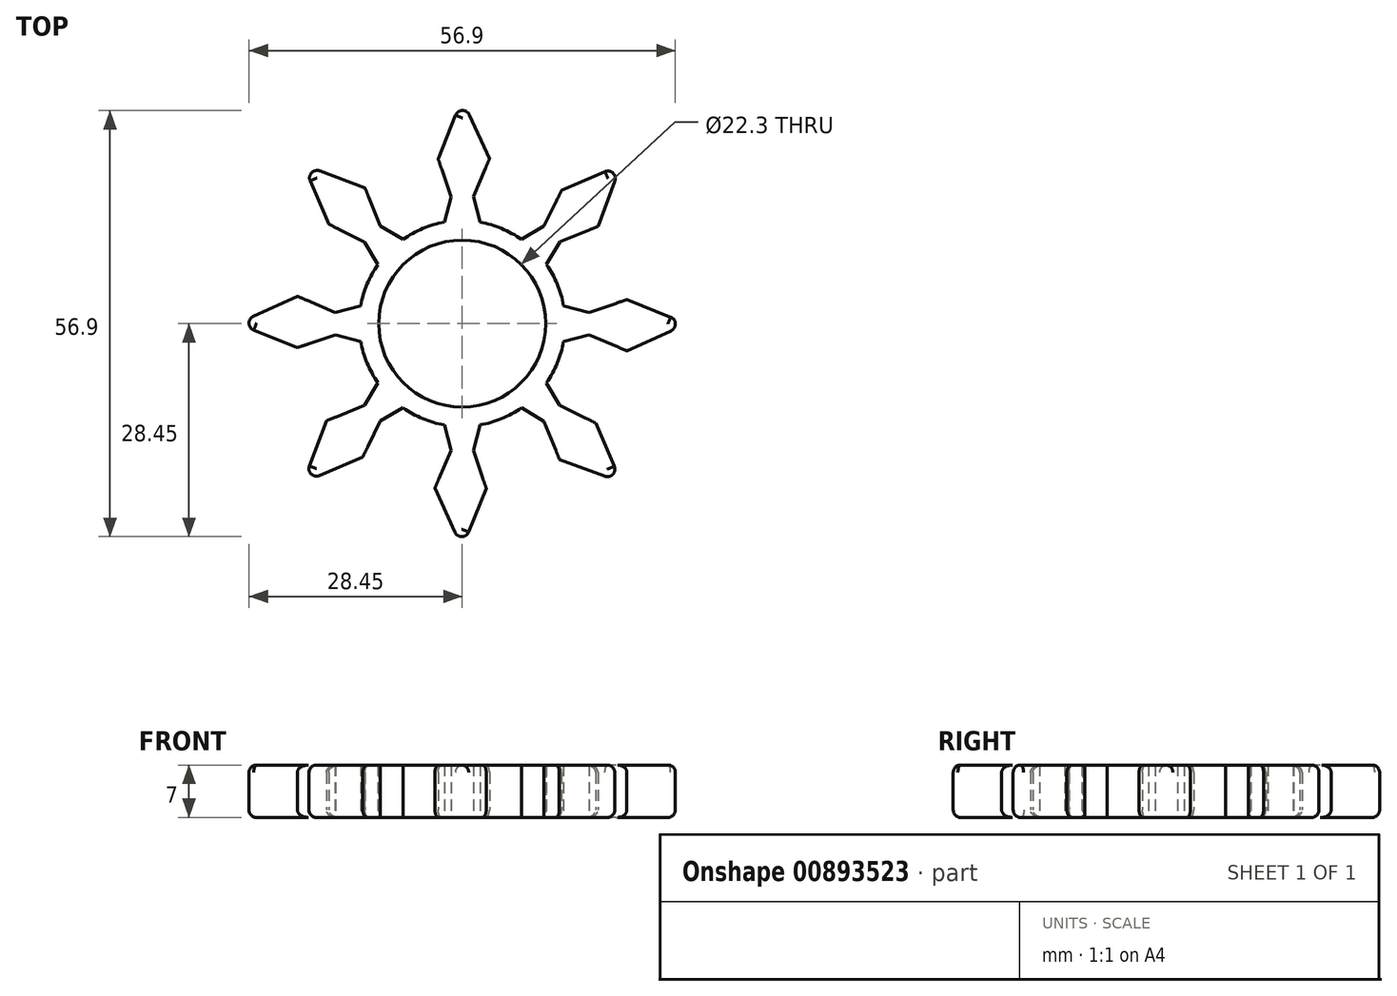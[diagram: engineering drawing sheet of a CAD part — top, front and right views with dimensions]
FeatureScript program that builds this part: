
annotation { "Feature Type Name" : "Feature", "Feature Type Description" : "" }
export const myFeature = defineFeature(function(context is Context, id is Id, definition is map)
    precondition{}
    {
        {
            var Q0;
            Q0=qCreatedBy(makeId("Top.planeOp"),FACE);
            var sketch = newSketch(context, id + "F0", { "sketchPlane" : qUnion([Q0])});
            skCircle(sketch, "E0", {"center": v(0, 0) * mm, "radius": 11.15 * mm});
            skLineSegment(sketch, "E1", {"start": v(0, 0) * mm, "end": v(0, 30) * mm, "construction": true});
            skLineSegment(sketch, "E2", {"start": v(0, 30) * mm, "end": v(16.85, 30) * mm, "construction": true});
            skLineSegment(sketch, "E3", {"start": v(0, 30) * mm, "end": v(-3.2, 22) * mm});
            skLineSegment(sketch, "E4", {"start": v(-3.2, 22) * mm, "end": v(3.65, 22) * mm, "construction": true});
            skLineSegment(sketch, "E5", {"start": v(0, 30) * mm, "end": v(3.65, 21.97) * mm});
            skLineSegment(sketch, "E6", {"start": v(-3.2, 22) * mm, "end": v(-1.5, 16.92) * mm});
            skLineSegment(sketch, "E7", {"start": v(3.65, 22) * mm, "end": v(1.5, 16.95) * mm});
            skLineSegment(sketch, "E8", {"start": v(1.5, 16.95) * mm, "end": v(0, 16.95) * mm, "construction": true});
            skLineSegment(sketch, "E9", {"start": v(0, 16.95) * mm, "end": v(-1.5, 16.92) * mm, "construction": true});
            skLineSegment(sketch, "E10", {"start": v(-1.5, 16.92) * mm, "end": v(-2.37, 13.54) * mm});
            skLineSegment(sketch, "E11", {"start": v(-2.3, 13.82) * mm, "end": v(0, 13.87) * mm, "construction": true});
            skLineSegment(sketch, "E12", {"start": v(-3.1, 10.71) * mm, "end": v(3.1, 10.71) * mm, "construction": true});
            skLineSegment(sketch, "E13", {"start": v(1.5, 16.95) * mm, "end": v(2.38, 13.54) * mm});
            skLineSegment(sketch, "E14.1.0", {"start": v(-21.21, 21.21) * mm, "end": v(-12.96, 18.12) * mm});
            skLineSegment(sketch, "E14.1.1", {"start": v(-21.21, 21.21) * mm, "end": v(-17.82, 13.29) * mm});
            skLineSegment(sketch, "E14.1.2", {"start": v(-17.82, 13.29) * mm, "end": v(-13.03, 10.9) * mm});
            skLineSegment(sketch, "E14.1.3", {"start": v(-12.97, 18.13) * mm, "end": v(-10.93, 13.05) * mm});
            skLineSegment(sketch, "E14.1.4", {"start": v(-10.93, 13.05) * mm, "end": v(-7.9, 11.25) * mm});
            skLineSegment(sketch, "E14.1.5", {"start": v(-13.03, 10.9) * mm, "end": v(-11.25, 7.9) * mm});
            skLineSegment(sketch, "E14.2.0", {"start": v(-30, 0) * mm, "end": v(-21.97, 3.65) * mm});
            skLineSegment(sketch, "E14.2.1", {"start": v(-30, 0) * mm, "end": v(-22, -3.2) * mm});
            skLineSegment(sketch, "E14.2.2", {"start": v(-22, -3.2) * mm, "end": v(-16.92, -1.5) * mm});
            skLineSegment(sketch, "E14.2.3", {"start": v(-22, 3.65) * mm, "end": v(-16.95, 1.5) * mm});
            skLineSegment(sketch, "E14.2.4", {"start": v(-16.95, 1.5) * mm, "end": v(-13.54, 2.38) * mm});
            skLineSegment(sketch, "E14.2.5", {"start": v(-16.92, -1.5) * mm, "end": v(-13.54, -2.37) * mm});
            skLineSegment(sketch, "E14.3.0", {"start": v(-21.21, -21.21) * mm, "end": v(-18.12, -12.96) * mm});
            skLineSegment(sketch, "E14.3.1", {"start": v(-21.21, -21.21) * mm, "end": v(-13.29, -17.82) * mm});
            skLineSegment(sketch, "E14.3.2", {"start": v(-13.29, -17.82) * mm, "end": v(-10.9, -13.03) * mm});
            skLineSegment(sketch, "E14.3.3", {"start": v(-18.13, -12.97) * mm, "end": v(-13.05, -10.93) * mm});
            skLineSegment(sketch, "E14.3.4", {"start": v(-13.05, -10.93) * mm, "end": v(-11.25, -7.9) * mm});
            skLineSegment(sketch, "E14.3.5", {"start": v(-10.9, -13.03) * mm, "end": v(-7.9, -11.25) * mm});
            skLineSegment(sketch, "E14.4.0", {"start": v(0, -30) * mm, "end": v(-3.65, -21.97) * mm});
            skLineSegment(sketch, "E14.4.1", {"start": v(0, -30) * mm, "end": v(3.2, -22) * mm});
            skLineSegment(sketch, "E14.4.2", {"start": v(3.2, -22) * mm, "end": v(1.5, -16.92) * mm});
            skLineSegment(sketch, "E14.4.3", {"start": v(-3.65, -22) * mm, "end": v(-1.5, -16.95) * mm});
            skLineSegment(sketch, "E14.4.4", {"start": v(-1.5, -16.95) * mm, "end": v(-2.38, -13.54) * mm});
            skLineSegment(sketch, "E14.4.5", {"start": v(1.5, -16.92) * mm, "end": v(2.37, -13.54) * mm});
            skLineSegment(sketch, "E14.5.0", {"start": v(21.21, -21.21) * mm, "end": v(12.96, -18.12) * mm});
            skLineSegment(sketch, "E14.5.1", {"start": v(21.21, -21.21) * mm, "end": v(17.82, -13.29) * mm});
            skLineSegment(sketch, "E14.5.2", {"start": v(17.82, -13.29) * mm, "end": v(13.03, -10.9) * mm});
            skLineSegment(sketch, "E14.5.3", {"start": v(12.97, -18.13) * mm, "end": v(10.93, -13.05) * mm});
            skLineSegment(sketch, "E14.5.4", {"start": v(10.93, -13.05) * mm, "end": v(7.9, -11.25) * mm});
            skLineSegment(sketch, "E14.5.5", {"start": v(13.03, -10.9) * mm, "end": v(11.25, -7.9) * mm});
            skLineSegment(sketch, "E14.6.0", {"start": v(30, 0) * mm, "end": v(21.97, -3.65) * mm});
            skLineSegment(sketch, "E14.6.1", {"start": v(30, 0) * mm, "end": v(22, 3.2) * mm});
            skLineSegment(sketch, "E14.6.2", {"start": v(22, 3.2) * mm, "end": v(16.92, 1.5) * mm});
            skLineSegment(sketch, "E14.6.3", {"start": v(22, -3.65) * mm, "end": v(16.95, -1.5) * mm});
            skLineSegment(sketch, "E14.6.4", {"start": v(16.95, -1.5) * mm, "end": v(13.54, -2.38) * mm});
            skLineSegment(sketch, "E14.6.5", {"start": v(16.92, 1.5) * mm, "end": v(13.54, 2.37) * mm});
            skLineSegment(sketch, "E14.7.0", {"start": v(21.21, 21.21) * mm, "end": v(18.12, 12.96) * mm});
            skLineSegment(sketch, "E14.7.1", {"start": v(21.21, 21.21) * mm, "end": v(13.29, 17.82) * mm});
            skLineSegment(sketch, "E14.7.2", {"start": v(13.29, 17.82) * mm, "end": v(10.9, 13.03) * mm});
            skLineSegment(sketch, "E14.7.3", {"start": v(18.13, 12.97) * mm, "end": v(13.05, 10.93) * mm});
            skLineSegment(sketch, "E14.7.4", {"start": v(13.05, 10.93) * mm, "end": v(11.25, 7.9) * mm});
            skLineSegment(sketch, "E14.7.5", {"start": v(10.9, 13.03) * mm, "end": v(7.9, 11.25) * mm});
            skCircle(sketch, "E15", {"center": v(0, 0) * mm, "radius": 13.74 * mm});
            skPoint(sketch, "E16.orphan", {"position": v(-5.38, 9.77) * mm});
            skPoint(sketch, "E17.orphan", {"position": v(-9.77, 5.38) * mm});
            skPoint(sketch, "E18.orphan", {"position": v(-10.71, 3.1) * mm});
            skPoint(sketch, "E19.orphan", {"position": v(-10.71, -3.1) * mm});
            skPoint(sketch, "E20.orphan", {"position": v(-9.77, -5.38) * mm});
            skPoint(sketch, "E21.orphan", {"position": v(-5.38, -9.77) * mm});
            skPoint(sketch, "E22.orphan", {"position": v(-3.1, -10.71) * mm});
            skPoint(sketch, "E23.orphan", {"position": v(3.1, -10.71) * mm});
            skPoint(sketch, "E24.orphan", {"position": v(5.38, -9.77) * mm});
            skPoint(sketch, "E25.orphan", {"position": v(9.77, -5.38) * mm});
            skPoint(sketch, "E26.orphan", {"position": v(10.71, -3.1) * mm});
            skPoint(sketch, "E27.orphan", {"position": v(9.77, 5.38) * mm});
            skPoint(sketch, "E28.orphan", {"position": v(5.38, 9.77) * mm});
            skPoint(sketch, "E29.orphan", {"position": v(10.71, 3.1) * mm});
            skSolve(sketch);
        }
        {
            var Q0;
            Q0=makeQuery(id+"F0.imprint","IMPRINT",FACE,{"disambiguationData":[TD([[makeQuery(id+"F0.imprint","IMPRINT",EDGE,{"derivedFrom":sQuery(id+"F0.wireOp",EDGE,"E0")}),-1.0]])]});
            var Q1;
            {var subQ4=sQuery(id+"F0.wireOp",EDGE,"E14.2.1");Q1=makeQuery(id+"F0.imprint","IMPRINT",FACE,{"disambiguationData":[TD([[makeQuery(id+"F0.imprint","IMPRINT",EDGE,{"derivedFrom":subQ4}),1.0]])]});}
            var Q2;
            {var subQ6=sQuery(id+"F0.wireOp",EDGE,"E14.1.1");Q2=makeQuery(id+"F0.imprint","IMPRINT",FACE,{"disambiguationData":[TD([[makeQuery(id+"F0.imprint","IMPRINT",EDGE,{"derivedFrom":subQ6}),1.0]])]});}
            var Q3;
            {var subQ4=sQuery(id+"F0.wireOp",EDGE,"E3");Q3=makeQuery(id+"F0.imprint","IMPRINT",FACE,{"disambiguationData":[TD([[makeQuery(id+"F0.imprint","IMPRINT",EDGE,{"derivedFrom":subQ4}),1.0]])]});}
            var Q4;
            {var subQ4=sQuery(id+"F0.wireOp",EDGE,"E14.7.1");Q4=makeQuery(id+"F0.imprint","IMPRINT",FACE,{"disambiguationData":[TD([[makeQuery(id+"F0.imprint","IMPRINT",EDGE,{"derivedFrom":subQ4}),1.0]])]});}
            var Q5;
            {var subQ4=sQuery(id+"F0.wireOp",EDGE,"E14.6.1");Q5=makeQuery(id+"F0.imprint","IMPRINT",FACE,{"disambiguationData":[TD([[makeQuery(id+"F0.imprint","IMPRINT",EDGE,{"derivedFrom":subQ4}),1.0]])]});}
            var Q6;
            {var subQ4=sQuery(id+"F0.wireOp",EDGE,"E14.5.1");Q6=makeQuery(id+"F0.imprint","IMPRINT",FACE,{"disambiguationData":[TD([[makeQuery(id+"F0.imprint","IMPRINT",EDGE,{"derivedFrom":subQ4}),1.0]])]});}
            var Q7;
            {var subQ6=sQuery(id+"F0.wireOp",EDGE,"E14.4.1");Q7=makeQuery(id+"F0.imprint","IMPRINT",FACE,{"disambiguationData":[TD([[makeQuery(id+"F0.imprint","IMPRINT",EDGE,{"derivedFrom":subQ6}),1.0]])]});}
            var Q8;
            {var subQ4=sQuery(id+"F0.wireOp",EDGE,"E14.3.1");Q8=makeQuery(id+"F0.imprint","IMPRINT",FACE,{"disambiguationData":[TD([[makeQuery(id+"F0.imprint","IMPRINT",EDGE,{"derivedFrom":subQ4}),1.0]])]});}
            extrude(context, id + "F1", {"entities" : qUnion([Q0, Q1, Q2, Q3, Q4, Q5, Q6, Q7, Q8]), "depth" : 7 * mm, "offsetDistance" : 25 * mm});
        }
        {
            var Q0;
            Q0=makeQuery(id+"F1.opExtrude","CAP_EDGE",EDGE,{"disambiguationData":[OSD([sQuery(id+"F0.wireOp",EDGE,"E14.2.1")])],"isStart":false});
            var Q1;
            Q1=makeQuery(id+"F1.opExtrude","CAP_EDGE",EDGE,{"disambiguationData":[OSD([sQuery(id+"F0.wireOp",EDGE,"E14.1.1")])],"isStart":false});
            var Q2;
            Q2=makeQuery(id+"F1.opExtrude","CAP_EDGE",EDGE,{"disambiguationData":[OSD([sQuery(id+"F0.wireOp",EDGE,"E3")])],"isStart":false});
            var Q3;
            Q3=makeQuery(id+"F1.opExtrude","CAP_EDGE",EDGE,{"disambiguationData":[OSD([sQuery(id+"F0.wireOp",EDGE,"E14.7.1")])],"isStart":false});
            var Q4;
            Q4=makeQuery(id+"F1.opExtrude","CAP_EDGE",EDGE,{"disambiguationData":[OSD([sQuery(id+"F0.wireOp",EDGE,"E14.6.1")])],"isStart":false});
            var Q5;
            Q5=makeQuery(id+"F1.opExtrude","CAP_EDGE",EDGE,{"disambiguationData":[OSD([sQuery(id+"F0.wireOp",EDGE,"E14.5.1")])],"isStart":false});
            var Q6;
            Q6=makeQuery(id+"F1.opExtrude","CAP_EDGE",EDGE,{"disambiguationData":[OSD([sQuery(id+"F0.wireOp",EDGE,"E14.4.1")])],"isStart":false});
            fillet(context, id + "F2", {"entities" : qUnion([Q0, Q1, Q2, Q3, Q4, Q5, Q6]), "radius" : 1 * mm, "tangentPropagation" : true, "allowEdgeOverflow" : false});
        }
        {
            var Q0;
            Q0=makeQuery(id+"F1.opExtrude","CAP_EDGE",EDGE,{"disambiguationData":[OSD([sQuery(id+"F0.wireOp",EDGE,"E14.1.0")])],"isStart":false});
            var Q1;
            Q1=makeQuery(id+"F1.opExtrude","CAP_EDGE",EDGE,{"disambiguationData":[OSD([sQuery(id+"F0.wireOp",EDGE,"E5")])],"isStart":false});
            var Q2;
            Q2=makeQuery(id+"F1.opExtrude","CAP_EDGE",EDGE,{"disambiguationData":[OSD([sQuery(id+"F0.wireOp",EDGE,"E14.7.0")])],"isStart":false});
            var Q3;
            Q3=makeQuery(id+"F1.opExtrude","CAP_EDGE",EDGE,{"disambiguationData":[OSD([sQuery(id+"F0.wireOp",EDGE,"E14.6.0")])],"isStart":false});
            var Q4;
            Q4=makeQuery(id+"F1.opExtrude","CAP_EDGE",EDGE,{"disambiguationData":[OSD([sQuery(id+"F0.wireOp",EDGE,"E14.5.0")])],"isStart":false});
            var Q5;
            Q5=makeQuery(id+"F1.opExtrude","CAP_EDGE",EDGE,{"disambiguationData":[OSD([sQuery(id+"F0.wireOp",EDGE,"E14.4.0")])],"isStart":false});
            var Q6;
            Q6=makeQuery(id+"F1.opExtrude","CAP_EDGE",EDGE,{"disambiguationData":[OSD([sQuery(id+"F0.wireOp",EDGE,"E14.3.0")])],"isStart":false});
            var Q7;
            Q7=makeQuery(id+"F1.opExtrude","CAP_EDGE",EDGE,{"disambiguationData":[OSD([sQuery(id+"F0.wireOp",EDGE,"E14.2.0")])],"isStart":false});
            fillet(context, id + "F3", {"entities" : qUnion([Q0, Q1, Q2, Q3, Q4, Q5, Q6, Q7]), "radius" : 1 * mm, "tangentPropagation" : true, "allowEdgeOverflow" : false});
        }
        {
            var Q0;
            Q0=makeQuery(id+"F1.opExtrude","CAP_EDGE",EDGE,{"disambiguationData":[OSD([sQuery(id+"F0.wireOp",EDGE,"E14.7.0")])],"isStart":true});
            var Q1;
            Q1=makeQuery(id+"F1.opExtrude","CAP_EDGE",EDGE,{"disambiguationData":[OSD([sQuery(id+"F0.wireOp",EDGE,"E5")])],"isStart":true});
            var Q2;
            Q2=makeQuery(id+"F1.opExtrude","CAP_EDGE",EDGE,{"disambiguationData":[OSD([sQuery(id+"F0.wireOp",EDGE,"E14.1.0")])],"isStart":true});
            var Q3;
            Q3=makeQuery(id+"F1.opExtrude","CAP_EDGE",EDGE,{"disambiguationData":[OSD([sQuery(id+"F0.wireOp",EDGE,"E14.2.0")])],"isStart":true});
            var Q4;
            Q4=makeQuery(id+"F1.opExtrude","CAP_EDGE",EDGE,{"disambiguationData":[OSD([sQuery(id+"F0.wireOp",EDGE,"E14.3.0")])],"isStart":true});
            var Q5;
            Q5=makeQuery(id+"F1.opExtrude","CAP_EDGE",EDGE,{"disambiguationData":[OSD([sQuery(id+"F0.wireOp",EDGE,"E14.4.0")])],"isStart":true});
            var Q6;
            Q6=makeQuery(id+"F1.opExtrude","CAP_EDGE",EDGE,{"disambiguationData":[OSD([sQuery(id+"F0.wireOp",EDGE,"E14.5.0")])],"isStart":true});
            var Q7;
            Q7=makeQuery(id+"F1.opExtrude","CAP_EDGE",EDGE,{"disambiguationData":[OSD([sQuery(id+"F0.wireOp",EDGE,"E14.6.0")])],"isStart":true});
            fillet(context, id + "F4", {"entities" : qUnion([Q0, Q1, Q2, Q3, Q4, Q5, Q6, Q7]), "radius" : 1 * mm, "tangentPropagation" : true, "allowEdgeOverflow" : false});
        }
        {
            var Q0;
            Q0=makeQuery(id+"F1.opExtrude","CAP_EDGE",EDGE,{"disambiguationData":[OSD([sQuery(id+"F0.wireOp",EDGE,"E14.3.1")])],"isStart":false});
            fillet(context, id + "F5", {"entities" : qUnion([Q0]), "radius" : 1 * mm, "tangentPropagation" : true, "allowEdgeOverflow" : false});
        }
        {
            var Q0;
            Q0=makeQuery(id+"F1.opExtrude","CAP_EDGE",EDGE,{"disambiguationData":[OSD([sQuery(id+"F0.wireOp",EDGE,"E0")])],"isStart":false});
            var Q1;
            Q1=makeQuery(id+"F1.opExtrude","CAP_EDGE",EDGE,{"disambiguationData":[OSD([sQuery(id+"F0.wireOp",EDGE,"E0")])],"isStart":true});
            fillet(context, id + "F6", {"entities" : qUnion([Q0, Q1]), "radius" : 0.2 * mm, "tangentPropagation" : true, "allowEdgeOverflow" : false});
        }
    });
